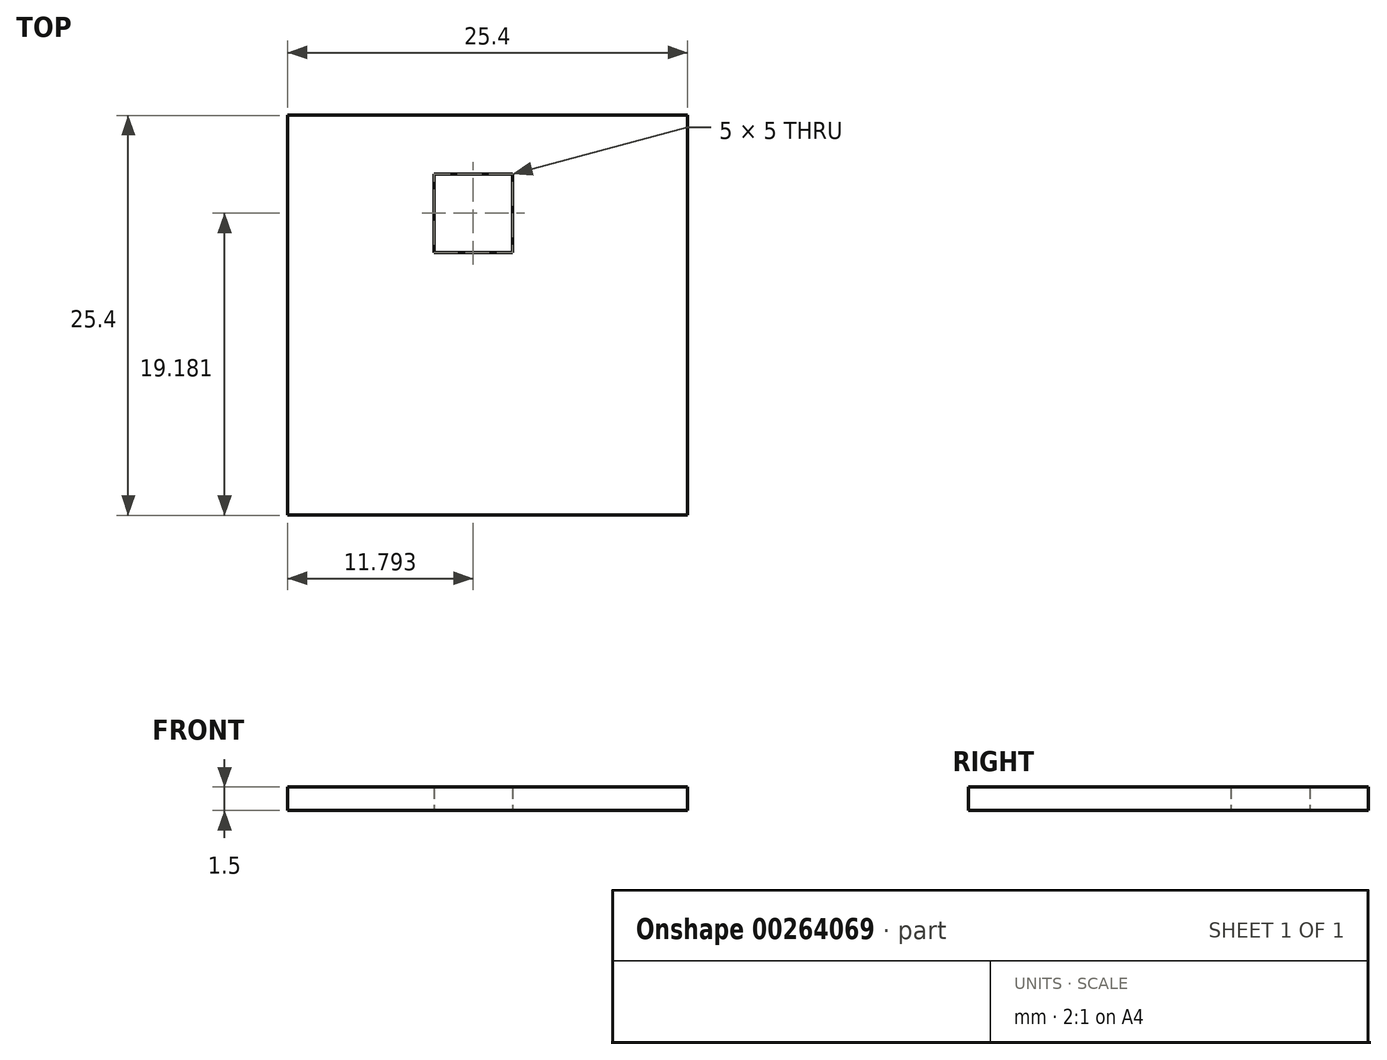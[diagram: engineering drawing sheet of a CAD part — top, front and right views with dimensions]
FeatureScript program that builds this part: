
annotation { "Feature Type Name" : "Feature", "Feature Type Description" : "" }
export const myFeature = defineFeature(function(context is Context, id is Id, definition is map)
    precondition{}
    {
        {
            var Q0;
            Q0=qCreatedBy(makeId("Top.planeOp"),FACE);
            var sketch = newSketch(context, id + "F0", { "sketchPlane" : qUnion([Q0])});
            skLineSegment(sketch, "E0.bottom", {"start": v(-13.08, 12.8) * mm, "end": v(12.32, 12.8) * mm});
            skLineSegment(sketch, "E0.top", {"start": v(-13.08, -12.6) * mm, "end": v(12.32, -12.6) * mm});
            skLineSegment(sketch, "E0.left", {"start": v(-13.08, 12.8) * mm, "end": v(-13.08, -12.6) * mm});
            skLineSegment(sketch, "E0.right", {"start": v(12.32, 12.8) * mm, "end": v(12.32, -12.6) * mm});
            skLineSegment(sketch, "E1.bottom", {"start": v(-3.79, 9.07) * mm, "end": v(1.21, 9.07) * mm});
            skLineSegment(sketch, "E1.top", {"start": v(-3.79, 4.07) * mm, "end": v(1.21, 4.07) * mm});
            skLineSegment(sketch, "E1.left", {"start": v(-3.79, 9.07) * mm, "end": v(-3.79, 4.07) * mm});
            skLineSegment(sketch, "E1.right", {"start": v(1.21, 9.07) * mm, "end": v(1.21, 4.07) * mm});
            skSolve(sketch);
        }
        {
            var Q0;
            Q0 = qSketchRegion(id + "F0", true);
            extrude(context, id + "F1", {"entities" : qUnion([Q0]), "depth" : 1.5 * mm});
        }
    });
